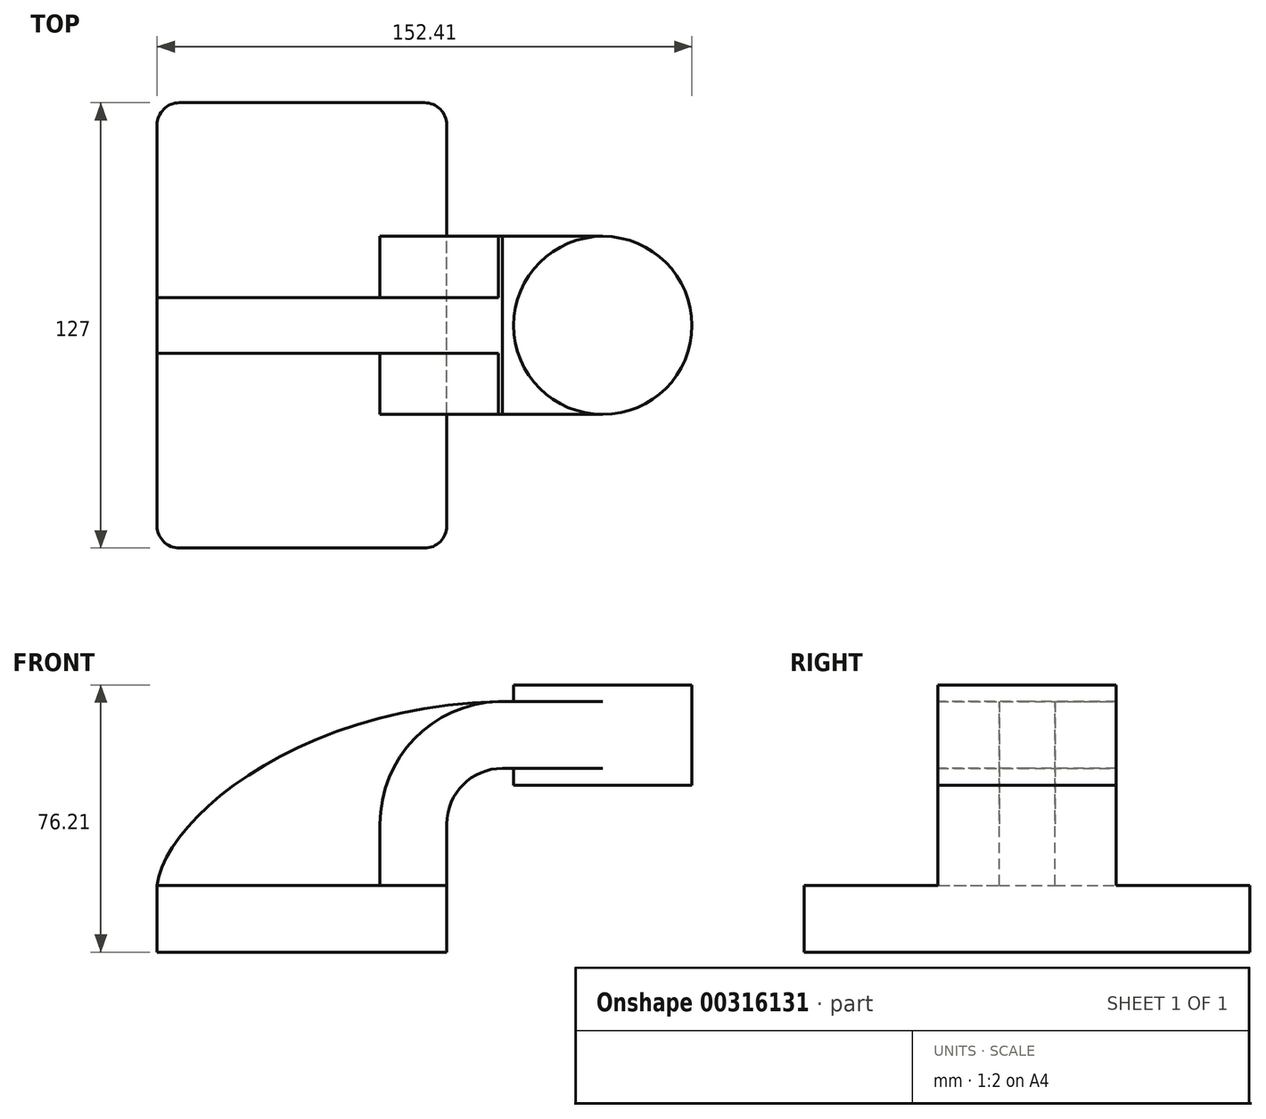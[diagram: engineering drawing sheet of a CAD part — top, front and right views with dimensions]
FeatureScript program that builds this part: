
annotation { "Feature Type Name" : "Feature", "Feature Type Description" : "" }
export const myFeature = defineFeature(function(context is Context, id is Id, definition is map)
    precondition{}
    {
        {
            var Q0;
            Q0=qCreatedBy(makeId("Front.planeOp"),FACE);
            var sketch = newSketch(context, id + "F0", { "sketchPlane" : qUnion([Q0])});
            skLineSegment(sketch, "E0.bottom", {"start": v(41.28, -9.52) * mm, "end": v(-41.27, -9.53) * mm});
            skLineSegment(sketch, "E0.top", {"start": v(41.27, 9.53) * mm, "end": v(-41.28, 9.53) * mm});
            skLineSegment(sketch, "E0.left", {"start": v(41.28, -9.52) * mm, "end": v(41.28, 9.53) * mm});
            skLineSegment(sketch, "E0.right", {"start": v(-41.27, -9.52) * mm, "end": v(-41.28, 9.53) * mm});
            skPoint(sketch, "E0.middle", {"position": v(0, 0) * mm});
            skLineSegment(sketch, "E1.bottom", {"start": v(111.12, 38.1) * mm, "end": v(60.32, 38.1) * mm});
            skLineSegment(sketch, "E1.top", {"start": v(111.12, 66.67) * mm, "end": v(60.32, 66.67) * mm});
            skLineSegment(sketch, "E1.left", {"start": v(111.12, 38.1) * mm, "end": v(111.12, 66.67) * mm});
            skLineSegment(sketch, "E1.right", {"start": v(60.32, 38.1) * mm, "end": v(60.32, 66.67) * mm});
            skPoint(sketch, "E1.middle", {"position": v(85.72, 52.39) * mm});
            skLineSegment(sketch, "E2", {"start": v(41.27, 9.53) * mm, "end": v(41.27, 27) * mm});
            skArc(sketch, "E3", {"start": v(41.27, 27) * mm, "mid": v(45.92, 38.23) * mm, "end": v(57.15, 42.88) * mm});
            skLineSegment(sketch, "E4", {"start": v(57.15, 42.88) * mm, "end": v(85.72, 42.88) * mm});
            skLineSegment(sketch, "E5.0", {"start": v(57.15, 61.93) * mm, "end": v(85.72, 61.93) * mm});
            skArc(sketch, "E5.1", {"start": v(22.23, 27) * mm, "mid": v(32.45, 51.7) * mm, "end": v(57.15, 61.93) * mm});
            skLineSegment(sketch, "E5.2", {"start": v(22.22, 9.53) * mm, "end": v(22.22, 27) * mm});
            skFitSpline(sketch, "E6", {"points": [v(-41.28, 9.53) * mm, v(57.15, 61.93) * mm], "startDerivative": vector(5.92, 56.3) * mm, "endDerivative": vector(171.45, 2.32) * mm});
            skPoint(sketch, "E7", {"position": v(85.72, 38.1) * mm});
            skLineSegment(sketch, "E8", {"start": v(85.72, 38.1) * mm, "end": v(85.72, 66.67) * mm});
            skSolve(sketch);
        }
        {
            var Q0;
            Q0=makeQuery(id+"F0.imprint","IMPRINT",FACE,{"disambiguationData":[TD([[makeQuery(id+"F0.imprint","IMPRINT",EDGE,{"derivedFrom":sQuery(id+"F0.wireOp",EDGE,"E0.bottom")}),-1.0]])]});
            extrude(context, id + "F1", {"entities" : qUnion([Q0]), "endBound" : BoundingType.SYMMETRIC, "depth" : 127 * mm});
        }
        {
            var Q0;
            {var subQ6=sQuery(id+"F0.wireOp",EDGE,"E2");Q0=makeQuery(id+"F0.imprint","IMPRINT",FACE,{"disambiguationData":[TD([[makeQuery(id+"F0.imprint","IMPRINT",EDGE,{"derivedFrom":subQ6}),1.0]])]});}
            var Q1;
            {var subQ0=sQuery(id+"F0.wireOp",EDGE,"E4");var subQ1=sQuery(id+"F0.wireOp",EDGE,"E1.right");var subQ2=makeQuery(id+"F0.imprint","INTERSECT",VERTEX,{"derivedFrom":[subQ1,subQ0]});Q1=makeQuery(id+"F0.imprint","IMPRINT",FACE,{"disambiguationData":[TD([[makeQuery(id+"F0.imprint","IMPRINT",EDGE,{"disambiguationData":[TD([[subQ2,-1.0]])],"derivedFrom":subQ1}),-1.0]])]});}
            extrude(context, id + "F2", {"entities" : qUnion([Q0, Q1]), "operationType" : NewBodyOperationType.ADD, "endBound" : BoundingType.SYMMETRIC, "depth" : 50.8 * mm});
        }
        {
            var Q0;
            {var subQ3=sQuery(id+"F0.wireOp",EDGE,"E5.2");Q0=makeQuery(id+"F0.imprint","IMPRINT",FACE,{"disambiguationData":[TD([[makeQuery(id+"F0.imprint","IMPRINT",EDGE,{"derivedFrom":subQ3}),1.0]])]});}
            extrude(context, id + "F3", {"entities" : qUnion([Q0]), "operationType" : NewBodyOperationType.ADD, "endBound" : BoundingType.SYMMETRIC, "depth" : 15.88 * mm});
        }
        {
            var Q0;
            {var subQ4=sQuery(id+"F0.wireOp",EDGE,"E1.left");Q0=makeQuery(id+"F0.imprint","IMPRINT",FACE,{"disambiguationData":[TD([[makeQuery(id+"F0.imprint","IMPRINT",EDGE,{"derivedFrom":subQ4}),1.0]])]});}
            var Q1;
            Q1=sQuery(id+"F0.wireOp",EDGE,"E8");
            revolve(context, id + "F4", {"operationType" : NewBodyOperationType.ADD, "entities" : qUnion([Q0]), "axis" : qUnion([Q1]), "revolveType" : RevolveType.FULL});
        }
        {
            var Q0;
            Q0=makeQuery(id+"F1.opExtrude","CAP_EDGE",EDGE,{"disambiguationData":[OSD([sQuery(id+"F0.wireOp",EDGE,"E0.left")])],"isStart":true});
            var Q1;
            Q1=makeQuery(id+"F1.opExtrude","CAP_EDGE",EDGE,{"disambiguationData":[OSD([sQuery(id+"F0.wireOp",EDGE,"E0.right")])],"isStart":true});
            var Q2;
            Q2=makeQuery(id+"F1.opExtrude","CAP_EDGE",EDGE,{"disambiguationData":[OSD([sQuery(id+"F0.wireOp",EDGE,"E0.left")])],"isStart":false});
            var Q3;
            Q3=makeQuery(id+"F1.opExtrude","CAP_EDGE",EDGE,{"disambiguationData":[OSD([sQuery(id+"F0.wireOp",EDGE,"E0.right")])],"isStart":false});
            fillet(context, id + "F5", {"entities" : qUnion([Q0, Q1, Q2, Q3]), "radius" : 6.35 * mm, "tangentPropagation" : true, "allowEdgeOverflow" : false});
        }
    });
